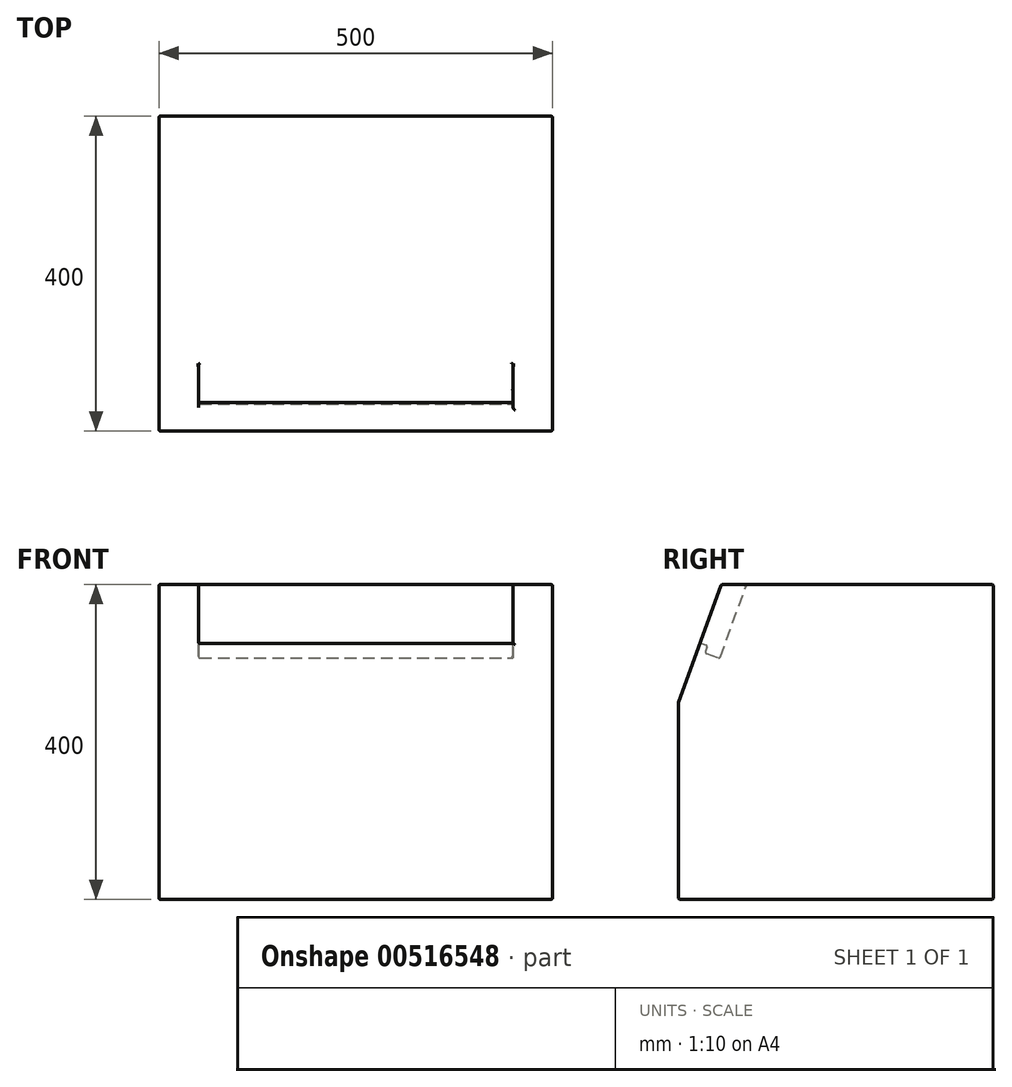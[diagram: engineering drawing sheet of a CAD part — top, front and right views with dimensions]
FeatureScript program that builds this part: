
annotation { "Feature Type Name" : "Feature", "Feature Type Description" : "" }
export const myFeature = defineFeature(function(context is Context, id is Id, definition is map)
    precondition{}
    {
        {
            var Q0;
            Q0=qCreatedBy(makeId("Right.planeOp"),FACE);
            var sketch = newSketch(context, id + "F0", { "sketchPlane" : qUnion([Q0])});
            skLineSegment(sketch, "E0", {"start": v(0, 0) * mm, "end": v(-400, 0) * mm});
            skLineSegment(sketch, "E1", {"start": v(-400, 0) * mm, "end": v(-400, 250) * mm});
            skLineSegment(sketch, "E2", {"start": v(-313.48, 400) * mm, "end": v(0, 400) * mm});
            skLineSegment(sketch, "E3", {"start": v(0, 400) * mm, "end": v(0, 0) * mm});
            skLineSegment(sketch, "E4", {"start": v(-372.45, 325.69) * mm, "end": v(-400, 250) * mm});
            skLineSegment(sketch, "E5", {"start": v(-372.45, 325.69) * mm, "end": v(-363.05, 322.27) * mm});
            skLineSegment(sketch, "E6", {"start": v(-363.05, 322.27) * mm, "end": v(-366.47, 312.87) * mm});
            skLineSegment(sketch, "E7", {"start": v(-366.47, 312.87) * mm, "end": v(-347.68, 306.03) * mm});
            skLineSegment(sketch, "E8", {"start": v(-347.68, 306.03) * mm, "end": v(-313.48, 400) * mm});
            skSolve(sketch);
        }
        {
            var Q0;
            Q0 = qSketchRegion(id + "F0", true);
            extrude(context, id + "F1", {"entities" : qUnion([Q0]), "depth" : 200 * mm, "offsetDistance" : 25 * mm});
        }
        {
            var Q0;
            Q0=makeQuery(id+"F1.opExtrude","CAP_FACE",FACE,{"disambiguationData":[OSD([sQuery(id+"F0.wireOp",EDGE,"E0"),sQuery(id+"F0.wireOp",EDGE,"E1"),sQuery(id+"F0.wireOp",EDGE,"E2"),sQuery(id+"F0.wireOp",EDGE,"E3"),sQuery(id+"F0.wireOp",EDGE,"E4"),sQuery(id+"F0.wireOp",EDGE,"E5"),sQuery(id+"F0.wireOp",EDGE,"E6"),sQuery(id+"F0.wireOp",EDGE,"E7"),sQuery(id+"F0.wireOp",EDGE,"E8")])],"isStart":false});
            var sketch = newSketch(context, id + "F2", { "sketchPlane" : qUnion([Q0])});
            skLineSegment(sketch, "E9", {"start": v(0, 400) * mm, "end": v(0, 0) * mm});
            skLineSegment(sketch, "E10", {"start": v(0, 0) * mm, "end": v(-400, 0) * mm});
            skLineSegment(sketch, "E11", {"start": v(-400, 0) * mm, "end": v(-400, 250) * mm});
            skLineSegment(sketch, "E12", {"start": v(-400, 250) * mm, "end": v(-345.4, 400) * mm});
            skLineSegment(sketch, "E13", {"start": v(0, 400) * mm, "end": v(-345.4, 400) * mm});
            skSolve(sketch);
        }
        {
            var Q0;
            Q0 = qSketchRegion(id + "F2", true);
            extrude(context, id + "F3", {"entities" : qUnion([Q0]), "operationType" : NewBodyOperationType.ADD, "depth" : 50 * mm, "offsetDistance" : 25 * mm});
        }
        {
            var Q0;
            Q0=makeQuery(id+"F1.opExtrude","SWEPT_BODY",BODY,{"disambiguationData":[OSD([sQuery(id+"F0.wireOp",EDGE,"E0"),sQuery(id+"F0.wireOp",EDGE,"E1"),sQuery(id+"F0.wireOp",EDGE,"E2"),sQuery(id+"F0.wireOp",EDGE,"E3"),sQuery(id+"F0.wireOp",EDGE,"E4"),sQuery(id+"F0.wireOp",EDGE,"E5"),sQuery(id+"F0.wireOp",EDGE,"E6"),sQuery(id+"F0.wireOp",EDGE,"E7"),sQuery(id+"F0.wireOp",EDGE,"E8")])]});
            var Q1;
            Q1=makeQuery(id+"F1.opExtrude","CAP_FACE",FACE,{"disambiguationData":[OSD([sQuery(id+"F0.wireOp",EDGE,"E0"),sQuery(id+"F0.wireOp",EDGE,"E1"),sQuery(id+"F0.wireOp",EDGE,"E2"),sQuery(id+"F0.wireOp",EDGE,"E3"),sQuery(id+"F0.wireOp",EDGE,"E4"),sQuery(id+"F0.wireOp",EDGE,"E5"),sQuery(id+"F0.wireOp",EDGE,"E6"),sQuery(id+"F0.wireOp",EDGE,"E7"),sQuery(id+"F0.wireOp",EDGE,"E8")])],"isStart":true});
            mirror(context, id + "F4", {"operationType" : NewBodyOperationType.ADD, "entities" : qUnion([Q0]), "mirrorPlane" : qUnion([Q1])});
        }
        {
            var Q0;
            {var subQ0=makeQuery(id+"F1.opExtrude","SWEPT_EDGE",EDGE,{"disambiguationData":[OSD([sQuery(id+"F0.wireOp",EDGE,"E4"),sQuery(id+"F0.wireOp",EDGE,"E5")])]});Q0=makeQuery(id+"F4.boolean.opBoolean","MERGE",EDGE,{"derivedFrom":[subQ0,makeQuery(id+"F4.opPattern","COPY",EDGE,{"derivedFrom":subQ0,"instanceName":"1"})]});}
            var Q1;
            {var subQ0=makeQuery(id+"F1.opExtrude","SWEPT_EDGE",EDGE,{"disambiguationData":[OSD([sQuery(id+"F0.wireOp",EDGE,"E5"),sQuery(id+"F0.wireOp",EDGE,"E6")])]});Q1=makeQuery(id+"F4.boolean.opBoolean","MERGE",EDGE,{"derivedFrom":[subQ0,makeQuery(id+"F4.opPattern","COPY",EDGE,{"derivedFrom":subQ0,"instanceName":"1"})]});}
            var Q2;
            {var subQ0=makeQuery(id+"F1.opExtrude","SWEPT_EDGE",EDGE,{"disambiguationData":[OSD([sQuery(id+"F0.wireOp",EDGE,"E6"),sQuery(id+"F0.wireOp",EDGE,"E7")])]});Q2=makeQuery(id+"F4.boolean.opBoolean","MERGE",EDGE,{"derivedFrom":[subQ0,makeQuery(id+"F4.opPattern","COPY",EDGE,{"derivedFrom":subQ0,"instanceName":"1"})]});}
            var Q3;
            {var subQ0=makeQuery(id+"F1.opExtrude","SWEPT_EDGE",EDGE,{"disambiguationData":[OSD([sQuery(id+"F0.wireOp",EDGE,"E7"),sQuery(id+"F0.wireOp",EDGE,"E8")])]});Q3=makeQuery(id+"F4.boolean.opBoolean","MERGE",EDGE,{"derivedFrom":[subQ0,makeQuery(id+"F4.opPattern","COPY",EDGE,{"derivedFrom":subQ0,"instanceName":"1"})]});}
            var Q4;
            Q4=makeQuery(id+"F1.opExtrude","CAP_EDGE",EDGE,{"disambiguationData":[OSD([sQuery(id+"F0.wireOp",EDGE,"E8")])],"isStart":false});
            var Q5;
            Q5=makeQuery(id+"F3.opExtrude","CAP_EDGE",EDGE,{"disambiguationData":[OSD([sQuery(id+"F2.wireOp",EDGE,"E12")])],"isStart":true});
            var Q6;
            {var subQ0=makeQuery(id+"F1.opExtrude","SWEPT_EDGE",EDGE,{"disambiguationData":[OSD([sQuery(id+"F0.wireOp",EDGE,"E2"),sQuery(id+"F0.wireOp",EDGE,"E8")])]});Q6=makeQuery(id+"F4.boolean.opBoolean","MERGE",EDGE,{"derivedFrom":[subQ0,makeQuery(id+"F4.opPattern","COPY",EDGE,{"derivedFrom":subQ0,"instanceName":"1"})]});}
            var Q7;
            Q7=makeQuery(id+"F4.opPattern","COPY",EDGE,{"derivedFrom":makeQuery(id+"F3.opExtrude","CAP_EDGE",EDGE,{"disambiguationData":[OSD([sQuery(id+"F2.wireOp",EDGE,"E12")])],"isStart":true}),"instanceName":"1"});
            var Q8;
            Q8=makeQuery(id+"F4.opPattern","COPY",EDGE,{"derivedFrom":makeQuery(id+"F3.opExtrude","CAP_EDGE",EDGE,{"disambiguationData":[OSD([sQuery(id+"F2.wireOp",EDGE,"E13")])],"isStart":true}),"instanceName":"1"});
            var Q9;
            Q9=makeQuery(id+"F4.opPattern","COPY",EDGE,{"derivedFrom":makeQuery(id+"F1.opExtrude","CAP_EDGE",EDGE,{"disambiguationData":[OSD([sQuery(id+"F0.wireOp",EDGE,"E7")])],"isStart":false}),"instanceName":"1"});
            var Q10;
            Q10=makeQuery(id+"F1.opExtrude","CAP_EDGE",EDGE,{"disambiguationData":[OSD([sQuery(id+"F0.wireOp",EDGE,"E7")])],"isStart":false});
            var Q11;
            Q11=makeQuery(id+"F4.opPattern","COPY",EDGE,{"derivedFrom":makeQuery(id+"F3.opExtrude","CAP_EDGE",EDGE,{"disambiguationData":[OSD([sQuery(id+"F2.wireOp",EDGE,"E13")])],"isStart":false}),"instanceName":"1"});
            var Q12;
            Q12=makeQuery(id+"F4.opPattern","COPY",EDGE,{"derivedFrom":makeQuery(id+"F3.opExtrude","SWEPT_EDGE",EDGE,{"disambiguationData":[OSD([sQuery(id+"F2.wireOp",EDGE,"E12"),sQuery(id+"F2.wireOp",EDGE,"E13")])]}),"instanceName":"1"});
            var Q13;
            Q13=makeQuery(id+"F4.opPattern","COPY",EDGE,{"derivedFrom":makeQuery(id+"F3.opExtrude","CAP_EDGE",EDGE,{"disambiguationData":[OSD([sQuery(id+"F2.wireOp",EDGE,"E12")])],"isStart":false}),"instanceName":"1"});
            var Q14;
            {var subQ0=makeQuery(id+"F3.boolean.opBoolean","MERGE",EDGE,{"derivedFrom":[makeQuery(id+"F1.opExtrude","SWEPT_EDGE",EDGE,{"disambiguationData":[OSD([sQuery(id+"F0.wireOp",EDGE,"E1"),sQuery(id+"F0.wireOp",EDGE,"E4")])]}),makeQuery(id+"F3.opExtrude","SWEPT_EDGE",EDGE,{"disambiguationData":[OSD([sQuery(id+"F2.wireOp",EDGE,"E11"),sQuery(id+"F2.wireOp",EDGE,"E12")])]})]});Q14=makeQuery(id+"F4.boolean.opBoolean","MERGE",EDGE,{"derivedFrom":[subQ0,makeQuery(id+"F4.opPattern","COPY",EDGE,{"derivedFrom":subQ0,"instanceName":"1"})]});}
            var Q15;
            Q15=makeQuery(id+"F4.opPattern","COPY",EDGE,{"derivedFrom":makeQuery(id+"F3.opExtrude","CAP_EDGE",EDGE,{"disambiguationData":[OSD([sQuery(id+"F2.wireOp",EDGE,"E11")])],"isStart":false}),"instanceName":"1"});
            var Q16;
            Q16=makeQuery(id+"F4.opPattern","COPY",EDGE,{"derivedFrom":makeQuery(id+"F3.opExtrude","CAP_EDGE",EDGE,{"disambiguationData":[OSD([sQuery(id+"F2.wireOp",EDGE,"E10")])],"isStart":false}),"instanceName":"1"});
            var Q17;
            Q17=makeQuery(id+"F4.opPattern","COPY",EDGE,{"derivedFrom":makeQuery(id+"F3.opExtrude","CAP_EDGE",EDGE,{"disambiguationData":[OSD([sQuery(id+"F2.wireOp",EDGE,"E9")])],"isStart":false}),"instanceName":"1"});
            var Q18;
            Q18=makeQuery(id+"F3.opExtrude","CAP_EDGE",EDGE,{"disambiguationData":[OSD([sQuery(id+"F2.wireOp",EDGE,"E13")])],"isStart":false});
            var Q19;
            Q19=makeQuery(id+"F3.opExtrude","CAP_EDGE",EDGE,{"disambiguationData":[OSD([sQuery(id+"F2.wireOp",EDGE,"E9")])],"isStart":false});
            var Q20;
            Q20=makeQuery(id+"F3.opExtrude","CAP_EDGE",EDGE,{"disambiguationData":[OSD([sQuery(id+"F2.wireOp",EDGE,"E11")])],"isStart":false});
            var Q21;
            Q21=makeQuery(id+"F3.opExtrude","CAP_EDGE",EDGE,{"disambiguationData":[OSD([sQuery(id+"F2.wireOp",EDGE,"E12")])],"isStart":false});
            var Q22;
            Q22=makeQuery(id+"F3.opExtrude","CAP_EDGE",EDGE,{"disambiguationData":[OSD([sQuery(id+"F2.wireOp",EDGE,"E10")])],"isStart":false});
            var Q23;
            {var subQ0=makeQuery(id+"F3.boolean.opBoolean","MERGE",EDGE,{"derivedFrom":[makeQuery(id+"F1.opExtrude","SWEPT_EDGE",EDGE,{"disambiguationData":[OSD([sQuery(id+"F0.wireOp",EDGE,"E0"),sQuery(id+"F0.wireOp",EDGE,"E1")])]}),makeQuery(id+"F3.opExtrude","SWEPT_EDGE",EDGE,{"disambiguationData":[OSD([sQuery(id+"F2.wireOp",EDGE,"E10"),sQuery(id+"F2.wireOp",EDGE,"E11")])]})]});Q23=makeQuery(id+"F4.boolean.opBoolean","MERGE",EDGE,{"derivedFrom":[subQ0,makeQuery(id+"F4.opPattern","COPY",EDGE,{"derivedFrom":subQ0,"instanceName":"1"})]});}
            var Q24;
            {var subQ0=makeQuery(id+"F3.boolean.opBoolean","MERGE",FACE,{"derivedFrom":[makeQuery(id+"F1.opExtrude","SWEPT_FACE",FACE,{"disambiguationData":[OSD([sQuery(id+"F0.wireOp",EDGE,"E0")])]}),makeQuery(id+"F3.opExtrude","SWEPT_FACE",FACE,{"disambiguationData":[OSD([sQuery(id+"F2.wireOp",EDGE,"E10")])]})]});Q24=makeQuery(id+"F4.boolean.opBoolean","MERGE",FACE,{"derivedFrom":[subQ0,makeQuery(id+"F4.opPattern","COPY",FACE,{"derivedFrom":subQ0,"instanceName":"1"})]});}
            var Q25;
            {var subQ0=makeQuery(id+"F3.boolean.opBoolean","MERGE",FACE,{"derivedFrom":[makeQuery(id+"F1.opExtrude","SWEPT_FACE",FACE,{"disambiguationData":[OSD([sQuery(id+"F0.wireOp",EDGE,"E3")])]}),makeQuery(id+"F3.opExtrude","SWEPT_FACE",FACE,{"disambiguationData":[OSD([sQuery(id+"F2.wireOp",EDGE,"E9")])]})]});Q25=makeQuery(id+"F4.boolean.opBoolean","MERGE",FACE,{"derivedFrom":[subQ0,makeQuery(id+"F4.opPattern","COPY",FACE,{"derivedFrom":subQ0,"instanceName":"1"})]});}
            var Q26;
            {var subQ0=makeQuery(id+"F1.opExtrude","SWEPT_FACE",FACE,{"disambiguationData":[OSD([sQuery(id+"F0.wireOp",EDGE,"E8")])]});Q26=makeQuery(id+"F4.boolean.opBoolean","MERGE",FACE,{"derivedFrom":[subQ0,makeQuery(id+"F4.opPattern","COPY",FACE,{"derivedFrom":subQ0,"instanceName":"1"})]});}
            var Q27;
            {var subQ0=makeQuery(id+"F3.boolean.opBoolean","MERGE",FACE,{"derivedFrom":[makeQuery(id+"F1.opExtrude","SWEPT_FACE",FACE,{"disambiguationData":[OSD([sQuery(id+"F0.wireOp",EDGE,"E2")])]}),makeQuery(id+"F3.opExtrude","SWEPT_FACE",FACE,{"disambiguationData":[OSD([sQuery(id+"F2.wireOp",EDGE,"E13")])]})]});Q27=makeQuery(id+"F4.boolean.opBoolean","MERGE",FACE,{"derivedFrom":[subQ0,makeQuery(id+"F4.opPattern","COPY",FACE,{"derivedFrom":subQ0,"instanceName":"1"})]});}
            var Q28;
            {var subQ0=makeQuery(id+"F3.boolean.opBoolean","MERGE",FACE,{"derivedFrom":[makeQuery(id+"F1.opExtrude","SWEPT_FACE",FACE,{"disambiguationData":[OSD([sQuery(id+"F0.wireOp",EDGE,"E4")])]}),makeQuery(id+"F3.opExtrude","SWEPT_FACE",FACE,{"disambiguationData":[OSD([sQuery(id+"F2.wireOp",EDGE,"E12")])]})]});Q28=makeQuery(id+"F4.boolean.opBoolean","MERGE",FACE,{"derivedFrom":[subQ0,makeQuery(id+"F4.opPattern","COPY",FACE,{"derivedFrom":subQ0,"instanceName":"1"})]});}
            var Q29;
            Q29=makeQuery(id+"F4.opPattern","COPY",FACE,{"derivedFrom":makeQuery(id+"F3.opExtrude","CAP_FACE",FACE,{"disambiguationData":[OSD([sQuery(id+"F2.wireOp",EDGE,"E9"),sQuery(id+"F2.wireOp",EDGE,"E10"),sQuery(id+"F2.wireOp",EDGE,"E11"),sQuery(id+"F2.wireOp",EDGE,"E12"),sQuery(id+"F2.wireOp",EDGE,"E13")])],"isStart":true}),"instanceName":"1"});
            fillet(context, id + "F5", {"entities" : qUnion([Q0, Q1, Q2, Q3, Q4, Q5, Q6, Q7, Q8, Q9, Q10, Q11, Q12, Q13, Q14, Q15, Q16, Q17, Q18, Q19, Q20, Q21, Q22, Q23, Q24, Q25, Q26, Q27, Q28, Q29]), "radius" : 2 * mm, "tangentPropagation" : true, "allowEdgeOverflow" : false});
        }
    });
